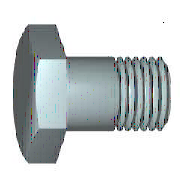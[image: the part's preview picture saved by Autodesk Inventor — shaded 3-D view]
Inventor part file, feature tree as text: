
AUTODESK INVENTOR PART (.ipt)
format: ipt  version: 2024 (Build 280153000, 153)  size: 206,336 bytes
history: native  units: mm (DEFAULTED — no unit token found)
features: extrude x1, chamfer x1, plane x1
ambient origin geometry x7: Origin, YZ Plane, XZ Plane, X Axis, Y Axis, Z Axis, Center Point
bodies: Solid1 (feature_tree), Body (feature_tree)
feature tree (3):
  extrude  "Head"  Depth=50.0mm
  chamfer  "Chamfer1"  Distance=26.0mm
  plane  "Work Plane1"
